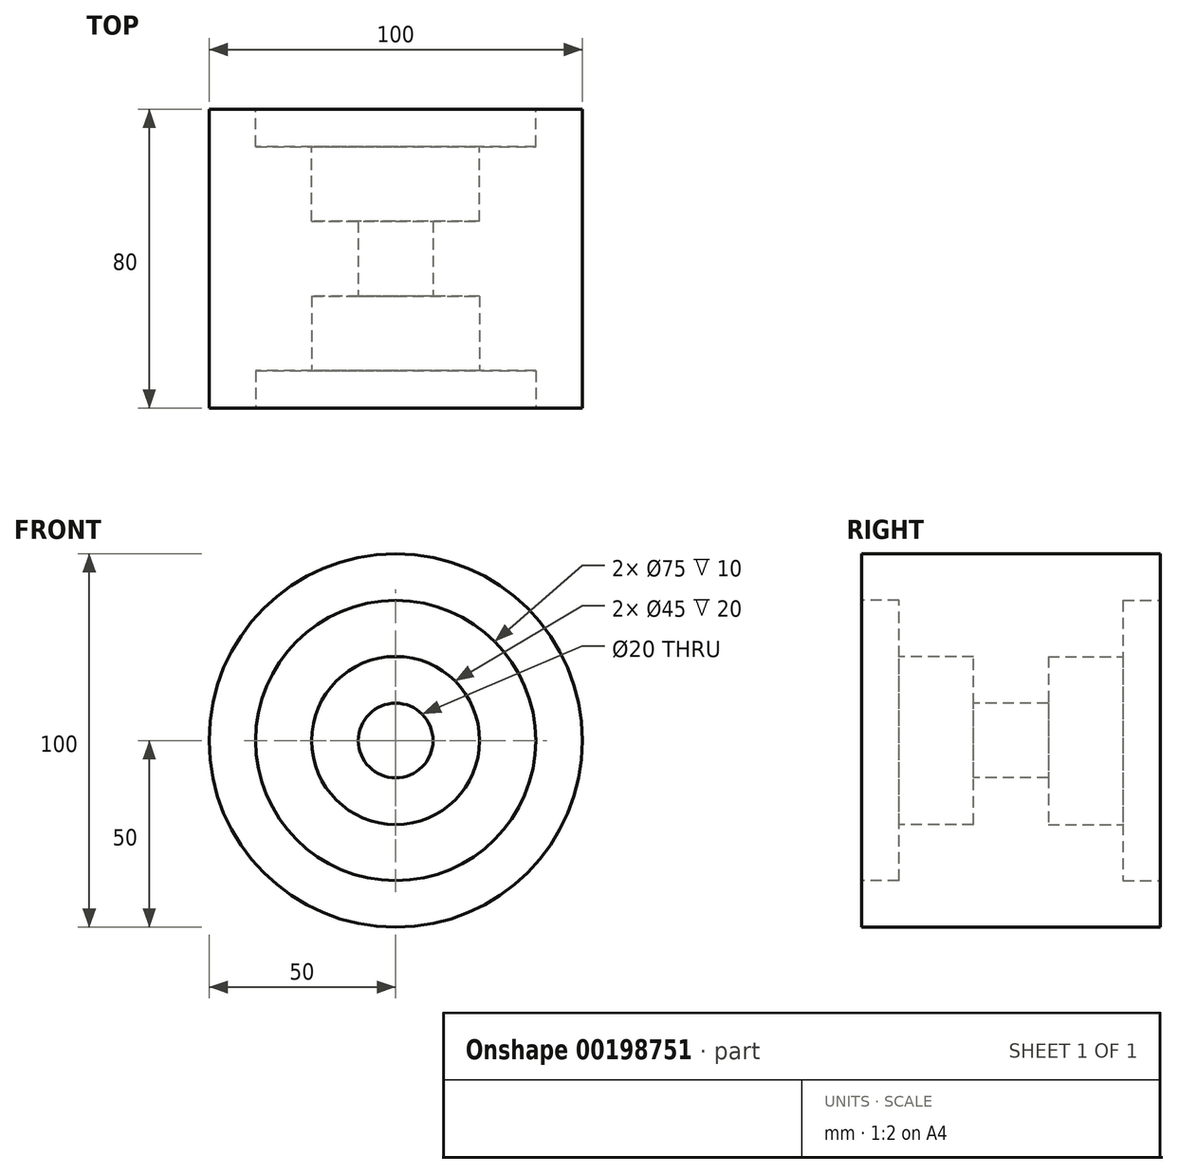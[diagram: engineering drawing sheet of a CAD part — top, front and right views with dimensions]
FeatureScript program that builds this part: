
annotation { "Feature Type Name" : "Feature", "Feature Type Description" : "" }
export const myFeature = defineFeature(function(context is Context, id is Id, definition is map)
    precondition{}
    {
        {
            var Q0;
            Q0=qCreatedBy(makeId("Front.planeOp"),FACE);
            var sketch = newSketch(context, id + "F0", { "sketchPlane" : qUnion([Q0])});
            skCircle(sketch, "E0", {"center": v(0, 0) * mm, "radius": 50 * mm});
            skSolve(sketch);
        }
        {
            var Q0;
            Q0 = qSketchRegion(id + "F0", true);
            extrude(context, id + "F1", {"entities" : qUnion([Q0]), "endBound" : BoundingType.SYMMETRIC, "depth" : 80 * mm});
        }
        {
            var Q0;
            Q0=makeQuery(id+"F1.opExtrude","CAP_FACE",FACE,{"disambiguationData":[OSD([sQuery(id+"F0.wireOp",EDGE,"E0")])],"isStart":false});
            var sketch = newSketch(context, id + "F2", { "sketchPlane" : qUnion([Q0])});
            skCircle(sketch, "E1", {"center": v(0, 0) * mm, "radius": 10 * mm});
            skSolve(sketch);
        }
        {
            var Q0;
            Q0 = qSketchRegion(id + "F2", true);
            extrude(context, id + "F3", {"entities" : qUnion([Q0]), "operationType" : NewBodyOperationType.REMOVE, "endBound" : BoundingType.THROUGH_ALL, "oppositeDirection" : true, "depth" : 25 * mm});
        }
        {
            var Q0;
            Q0=makeQuery(id+"F1.opExtrude","CAP_FACE",FACE,{"disambiguationData":[OSD([sQuery(id+"F0.wireOp",EDGE,"E0")])],"isStart":false});
            var sketch = newSketch(context, id + "F4", { "sketchPlane" : qUnion([Q0])});
            skCircle(sketch, "E2", {"center": v(0, 0) * mm, "radius": 37.5 * mm});
            skSolve(sketch);
        }
        {
            var Q0;
            Q0 = qSketchRegion(id + "F4", true);
            extrude(context, id + "F5", {"entities" : qUnion([Q0]), "operationType" : NewBodyOperationType.REMOVE, "oppositeDirection" : true, "depth" : 10 * mm});
        }
        {
            var Q0;
            Q0=makeQuery(id+"F5.boolean.opBoolean","COPY",FACE,{"derivedFrom":makeQuery(id+"F5.opExtrude","CAP_FACE",FACE,{"disambiguationData":[OSD([sQuery(id+"F4.wireOp",EDGE,"E2")])],"isStart":false})});
            var sketch = newSketch(context, id + "F6", { "sketchPlane" : qUnion([Q0])});
            skCircle(sketch, "E3", {"center": v(0, 0) * mm, "radius": 22.5 * mm});
            skSolve(sketch);
        }
        {
            var Q0;
            Q0 = qSketchRegion(id + "F6", true);
            extrude(context, id + "F7", {"entities" : qUnion([Q0]), "operationType" : NewBodyOperationType.REMOVE, "oppositeDirection" : true, "depth" : 20 * mm});
        }
        {
            var Q0;
            Q0=makeQuery(id+"F1.opExtrude","CAP_FACE",FACE,{"disambiguationData":[OSD([sQuery(id+"F0.wireOp",EDGE,"E0")])],"isStart":true});
            var sketch = newSketch(context, id + "F8", { "sketchPlane" : qUnion([Q0])});
            skCircle(sketch, "E4", {"center": v(0, 0) * mm, "radius": 37.5 * mm});
            skSolve(sketch);
        }
        {
            var Q0;
            Q0 = qSketchRegion(id + "F8", true);
            extrude(context, id + "F9", {"entities" : qUnion([Q0]), "operationType" : NewBodyOperationType.REMOVE, "oppositeDirection" : true, "depth" : 10 * mm});
        }
        {
            var Q0;
            Q0=makeQuery(id+"F9.boolean.opBoolean","COPY",FACE,{"derivedFrom":makeQuery(id+"F9.opExtrude","CAP_FACE",FACE,{"disambiguationData":[OSD([sQuery(id+"F8.wireOp",EDGE,"E4")])],"isStart":false})});
            var sketch = newSketch(context, id + "F10", { "sketchPlane" : qUnion([Q0])});
            skCircle(sketch, "E5", {"center": v(0, 0) * mm, "radius": 22.5 * mm});
            skSolve(sketch);
        }
        {
            var Q0;
            Q0 = qSketchRegion(id + "F10", true);
            extrude(context, id + "F11", {"entities" : qUnion([Q0]), "operationType" : NewBodyOperationType.REMOVE, "oppositeDirection" : true, "depth" : 20 * mm});
        }
    });
